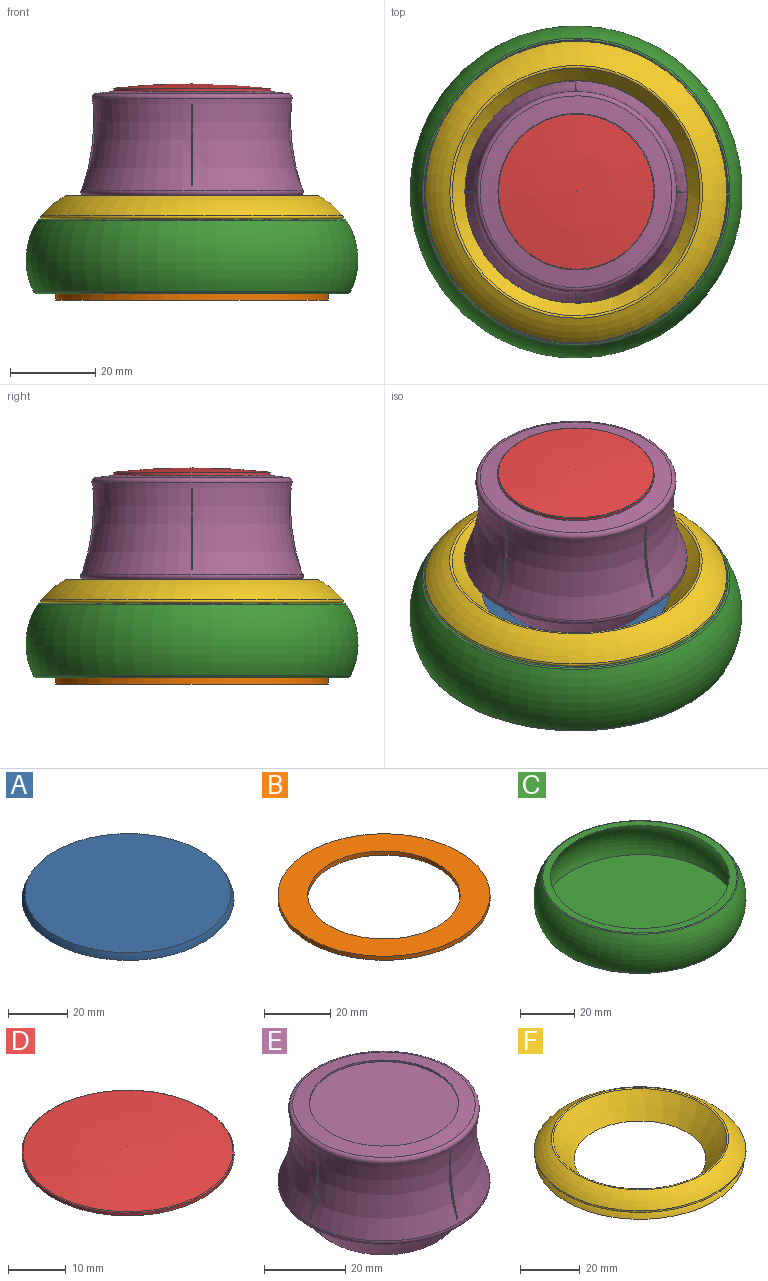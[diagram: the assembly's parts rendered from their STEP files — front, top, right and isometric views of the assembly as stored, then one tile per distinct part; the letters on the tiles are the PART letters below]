
ASSEMBLY  parts=6 mates=5
PART A: 3 faces, bbox 79x79x10.1 mm
  f0: plane 71.82x71.82mm, normal (0,0,-1), area 4050.7mm2, adj f1
  f1: torus R=22.25mm, axis (0,0,-1), area 601.4mm2, adj f0,f2
  f2: plane 69.8x69.8mm, normal (0,0,1), area 3826mm2, adj f1
PART B: 4 faces, bbox 64x64x1.5 mm
  f0: cylinder r=32mm len=64mm, axis (0,0,-1), area 301.6mm2, adj f1,f3
  f1: plane 64x64mm, normal (0,0,1), area 1555.1mm2, adj f0,f2
  f2: cylinder r=23mm len=46mm, axis (0,0,-1), area 216.8mm2, adj f1,f3
  f3: plane 64x64mm, normal (0,0,-1), area 1555.1mm2, adj f0,f2
PART C: 7 faces, bbox 84.4x84.4x23.8 mm
  f0: plane 72.78x72.78mm, normal (0,0,-1), area 4160.2mm2, adj f1
  f1: torus R=36.39mm, axis (0,0,-1), area 258.4mm2, adj f0,f2
  f2: torus R=22.25mm, axis (0,0,-1), area 4213.2mm2, adj f1,f3
  f3: torus R=35.74mm, axis (0,0,-1), area 110.6mm2, adj f2,f4
  f4: plane 71.47x71.47mm, normal (0,0,1), area 629.7mm2, adj f3,f5
  f5: torus R=22.25mm, axis (0,0,-1), area 3588.7mm2, adj f4,f6
  f6: plane 70.84x70.84mm, normal (0,0,1), area 3941.8mm2, adj f5
PART D: 4 faces, bbox 39.8x39.8x1.7 mm
  f0: plane 36.75x36.75mm, normal (0,0,-1), area 1060.7mm2, adj f1
  f1: cylinder r=18.38mm len=36.75mm, axis (0,0,-1), area 67.4mm2, adj f0,f2
  f2: torus R=18.19mm, axis (0,0,-1), area 31.6mm2, adj f1,f3
  f3: sphere r=170.25mm, area 1044.5mm2, adj f2
PART E: 20 faces, bbox 71.4x71.4x49.7 mm
  f0: plane 36.29x36.29mm, normal (0,0,-1), area 1034.1mm2, adj f1
  f1: cone r=25.13mm half-angle=40deg, axis (0,0,1), area 1478.7mm2, adj f0,f2
  f2: torus R=25.14mm, axis (0,0,-1), area 326.5mm2, adj f1,f3
  f3: torus R=57.81mm, axis (0,0,-1), area 3255.2mm2, adj f2,f4,f8,f9,f10,f11,f12,f13
  f4: torus R=22.51mm, axis (0,0,-1), area 257.5mm2, adj f3,f5
  f5: sphere r=170mm, area 534.9mm2, adj f4,f6
  f6: cylinder r=18.38mm len=36.75mm, axis (0,0,-1), area 57.8mm2, adj f5,f7
  f7: plane 36.75x36.75mm, normal (0,0,1), area 1060.7mm2, adj f6
  f8: cylinder r=50mm len=19.17mm, axis (0,1,0), area 4.9mm2, adj f3,f9,f10
  f9: plane 19.17x2.89mm, normal (0,-1,0), area 5.4mm2, adj f3,f8
  f10: plane 19.17x2.89mm, normal (0,1,0), area 5.4mm2, adj f3,f8
  f11: cylinder r=50mm len=19.17mm, axis (-1,0,0), area 4.9mm2, adj f3,f12,f13
  f12: plane 19.17x2.89mm, normal (1,0,0), area 5.4mm2, adj f3,f11
  f13: plane 19.17x2.89mm, normal (-1,0,0), area 5.4mm2, adj f3,f11
  f14: cylinder r=50mm len=19.17mm, axis (0,-1,0), area 4.9mm2, adj f3,f15,f16
  f15: plane 19.17x2.89mm, normal (0,1,0), area 5.4mm2, adj f3,f14
  f16: plane 19.17x2.89mm, normal (0,-1,0), area 5.4mm2, adj f3,f14
  f17: cylinder r=50mm len=19.17mm, axis (1,0,0), area 4.9mm2, adj f3,f18,f19
  f18: plane 19.17x2.89mm, normal (-1,0,0), area 5.4mm2, adj f3,f17
  f19: plane 19.17x2.89mm, normal (1,0,0), area 5.4mm2, adj f3,f17
PART F: 7 faces, bbox 84.4x84.4x16.7 mm
  f0: torus R=22.25mm, axis (0,0,-1), area 780.8mm2, adj f1,f6
  f1: plane 70.01x70.01mm, normal (0,0,-1), area 467.7mm2, adj f0,f2
  f2: torus R=35.01mm, axis (0,0,-1), area 248.8mm2, adj f1,f3
  f3: torus R=22.25mm, axis (0,0,-1), area 1527mm2, adj f2,f4
  f4: torus R=29.45mm, axis (0,0,-1), area 122.8mm2, adj f3,f5
  f5: cone r=29.07mm half-angle=40deg, axis (0,0,1), area 1745.7mm2, adj f4,f6
  f6: plane 69.8x69.8mm, normal (0,0,-1), area 2293.5mm2, adj f0,f5
PLACE A t=(0,0,1.5)mm
PLACE B t=(0,0,1.5)mm
PLACE C t=(0,0,1.5)mm
PLACE D t=(0,0,2)mm
PLACE E t=(0,0,1.5)mm
PLACE F t=(0,0,1.5)mm
MATE fastened D.f1 <-> E.f1  axis (0,0,-1) through (0,0,48.99)mm
MATE fastened C.f1 <-> B.f0  axis (0,0,-1) through (0,0,1.5)mm
MATE fastened E.f1 <-> A.f1  axis (0,0,-1) through (0,0,16)mm
MATE fastened F.f0 <-> A.f1  axis (0,0,-1) through (0,0,16)mm
MATE fastened F.f0 <-> C.f1  axis (0,0,-1) through (0,0,19)mm
